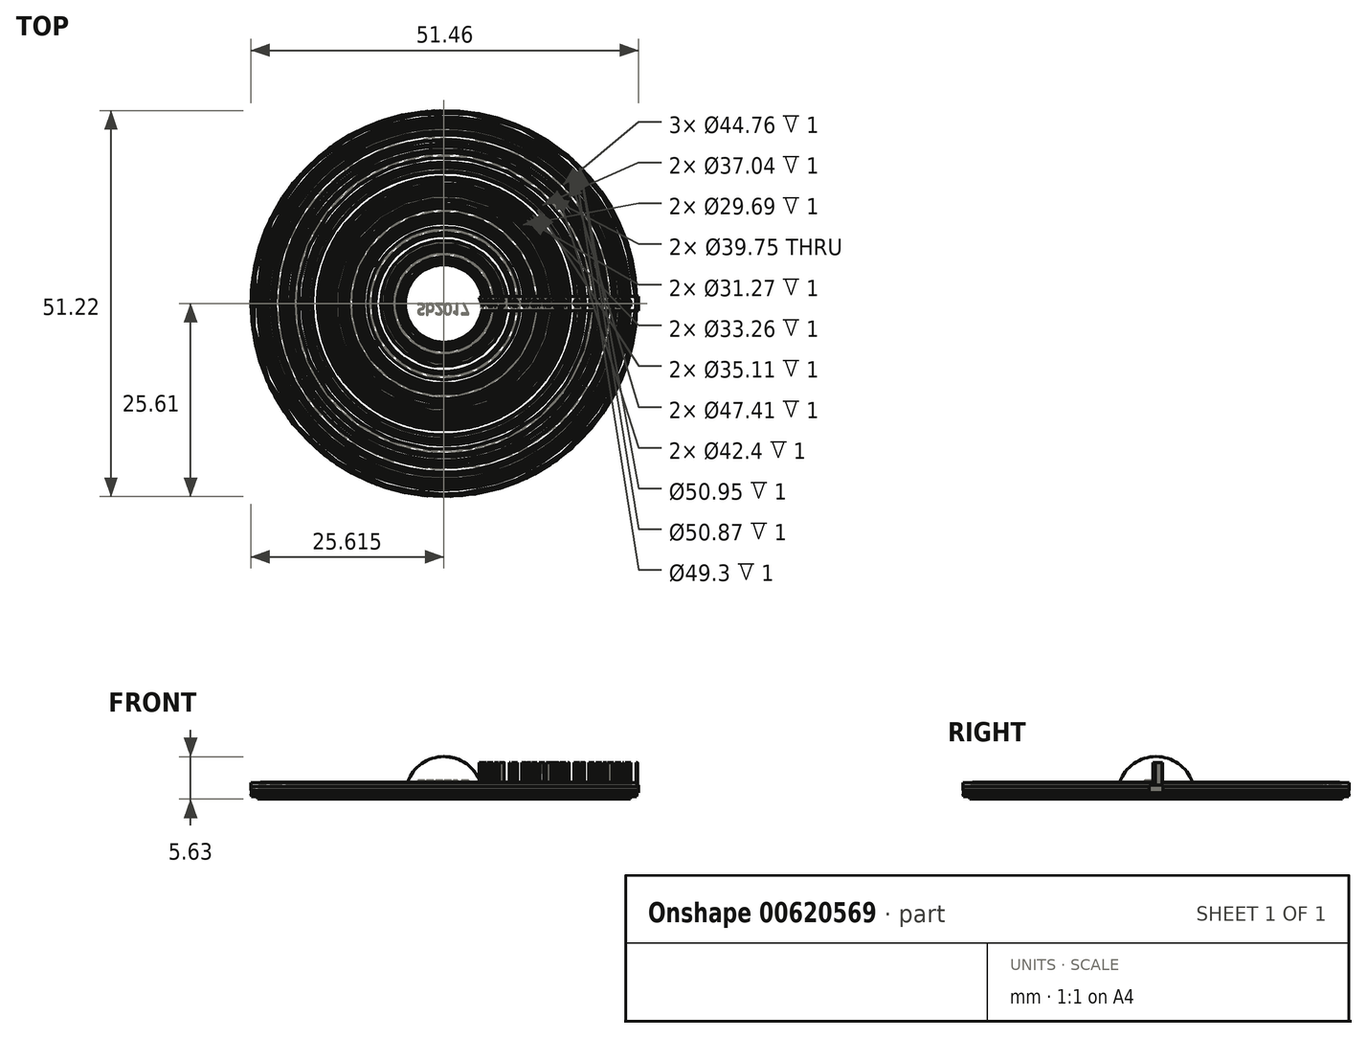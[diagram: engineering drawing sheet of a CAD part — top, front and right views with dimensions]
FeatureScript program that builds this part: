
annotation { "Feature Type Name" : "Feature", "Feature Type Description" : "" }
export const myFeature = defineFeature(function(context is Context, id is Id, definition is map)
    precondition{}
    {
        {
            var Q0;
            Q0=qCreatedBy(makeId("Front.planeOp"),FACE);
            var sketch = newSketch(context, id + "F0", { "sketchPlane" : qUnion([Q0])});
            skPoint(sketch, "E0", {"position": v(-19.14, 21.87) * mm});
            skText(sketch, "E1", { "text": "Vers le transfini et au-delà !", "fontName": "OpenSans-Regular.ttf"});
            skLineSegment(sketch, "E2", {"start": v(-14, 20.73) * mm, "end": v(-19.14, 20.73) * mm});
            skLineSegment(sketch, "E3", {"start": v(-14.14, 20.73) * mm, "end": v(-19.14, 20.73) * mm});
            skLineSegment(sketch, "E4", {"start": v(-19.14, 20.73) * mm, "end": v(-19.14, 25.86) * mm});
            skArc(sketch, "E5", {"start": v(-14, 20.73) * mm, "mid": v(-15.5, 24.36) * mm, "end": v(-19.14, 25.86) * mm});
            skLineSegment(sketch, "E6", {"start": v(-19.14, 25.86) * mm, "end": v(-19.14, 20.73) * mm});
            const initialGuessF0  = {"E1": [-0.014, 0.02073, 1, 0, 0.00117]};
            skSetInitialGuess(sketch, initialGuessF0);
            skSolve(sketch);
        }
        {
            var Q0;
            Q0=qSketchRegion(id+"F0",true);
            var Q1;
            Q1=sQuery(id+"F0.wireOp",EDGE,"E6");
            revolve(context, id + "F1", {"entities" : qUnion([Q0]), "axis" : qUnion([Q1]), "revolveType" : RevolveType.FULL});
        }
        {
            var Q0;
            Q0=makeQuery(id+"F1.opRevolve","SWEPT_FACE",FACE,{"disambiguationData":[OSD([sQuery(id+"F0.wireOp",EDGE,"E1.sketch_text.stroke-156")])]});
            var sketch = newSketch(context, id + "F2", { "sketchPlane" : qUnion([Q0])});
            skLineSegment(sketch, "E7.bottom", {"start": v(-14.29, 0.94) * mm, "end": v(6.71, 0.94) * mm});
            skLineSegment(sketch, "E7.top", {"start": v(-14.29, -0.94) * mm, "end": v(6.71, -0.94) * mm});
            skLineSegment(sketch, "E7.left", {"start": v(-14.29, 0.94) * mm, "end": v(-14.29, -0.94) * mm});
            skLineSegment(sketch, "E7.right", {"start": v(6.71, 0.94) * mm, "end": v(6.71, -0.94) * mm});
            skSolve(sketch);
        }
        {
            var Q0;
            Q0=makeQuery(id+"F2.imprint","IMPRINT",FACE,{"disambiguationData":[TD([[makeQuery(id+"F2.imprint","IMPRINT",EDGE,{"derivedFrom":sQuery(id+"F2.wireOp",EDGE,"E7.bottom")}),-1.0]])]});
            var Q1;
            Q1=makeQuery(id+"F1.opRevolve","SWEPT_FACE",FACE,{"disambiguationData":[OSD([sQuery(id+"F0.wireOp",EDGE,"E1.sketch_text.stroke-278")])]});
            var Q2;
            Q2=makeQuery(id+"F1.opRevolve","SWEPT_FACE",FACE,{"disambiguationData":[OSD([sQuery(id+"F0.wireOp",EDGE,"E1.sketch_text.stroke-280")])]});
            var Q3;
            Q3=makeQuery(id+"F1.opRevolve","SWEPT_FACE",FACE,{"disambiguationData":[OSD([sQuery(id+"F0.wireOp",EDGE,"E1.sketch_text.stroke-227")])]});
            var Q4;
            Q4=makeQuery(id+"F1.opRevolve","SWEPT_FACE",FACE,{"disambiguationData":[OSD([sQuery(id+"F0.wireOp",EDGE,"E1.sketch_text.stroke-238")])]});
            var Q5;
            Q5=makeQuery(id+"F1.opRevolve","SWEPT_FACE",FACE,{"disambiguationData":[OSD([sQuery(id+"F0.wireOp",EDGE,"E1.sketch_text.stroke-341")])]});
            var Q6;
            Q6=makeQuery(id+"F1.opRevolve","SWEPT_FACE",FACE,{"disambiguationData":[OSD([sQuery(id+"F0.wireOp",EDGE,"E1.sketch_text.stroke-345")])]});
            var Q7;
            Q7=makeQuery(id+"F1.opRevolve","SWEPT_FACE",FACE,{"disambiguationData":[OSD([sQuery(id+"F0.wireOp",EDGE,"E1.sketch_text.stroke-274")])]});
            var Q8;
            Q8=makeQuery(id+"F1.opRevolve","SWEPT_FACE",FACE,{"disambiguationData":[OSD([sQuery(id+"F0.wireOp",EDGE,"E1.sketch_text.stroke-282")])]});
            var Q9;
            Q9=makeQuery(id+"F1.opRevolve","SWEPT_FACE",FACE,{"disambiguationData":[OSD([sQuery(id+"F0.wireOp",EDGE,"E1.sketch_text.stroke-229")])]});
            var Q10;
            Q10=makeQuery(id+"F1.opRevolve","SWEPT_FACE",FACE,{"disambiguationData":[OSD([sQuery(id+"F0.wireOp",EDGE,"E1.sketch_text.stroke-255")])]});
            var Q11;
            Q11=makeQuery(id+"F1.opRevolve","SWEPT_FACE",FACE,{"disambiguationData":[OSD([sQuery(id+"F0.wireOp",EDGE,"E1.sketch_text.stroke-329")])]});
            var Q12;
            Q12=makeQuery(id+"F1.opRevolve","SWEPT_FACE",FACE,{"disambiguationData":[OSD([sQuery(id+"F0.wireOp",EDGE,"E1.sketch_text.stroke-319")])]});
            var Q13;
            Q13=makeQuery(id+"F1.opRevolve","SWEPT_FACE",FACE,{"disambiguationData":[OSD([sQuery(id+"F0.wireOp",EDGE,"E1.sketch_text.stroke-331")])]});
            var Q14;
            Q14=makeQuery(id+"F1.opRevolve","SWEPT_FACE",FACE,{"disambiguationData":[OSD([sQuery(id+"F0.wireOp",EDGE,"E1.sketch_text.stroke-418")])]});
            var Q15;
            Q15=makeQuery(id+"F1.opRevolve","SWEPT_FACE",FACE,{"disambiguationData":[OSD([sQuery(id+"F0.wireOp",EDGE,"E1.sketch_text.stroke-416")])]});
            var Q16;
            Q16=makeQuery(id+"F1.opRevolve","SWEPT_FACE",FACE,{"disambiguationData":[OSD([sQuery(id+"F0.wireOp",EDGE,"E1.sketch_text.stroke-379")])]});
            var Q17;
            Q17=makeQuery(id+"F1.opRevolve","SWEPT_FACE",FACE,{"disambiguationData":[OSD([sQuery(id+"F0.wireOp",EDGE,"E1.sketch_text.stroke-412")])]});
            var Q18;
            Q18=makeQuery(id+"F1.opRevolve","SWEPT_FACE",FACE,{"disambiguationData":[OSD([sQuery(id+"F0.wireOp",EDGE,"E1.sketch_text.stroke-205")])]});
            var Q19;
            Q19=makeQuery(id+"F1.opRevolve","SWEPT_FACE",FACE,{"disambiguationData":[OSD([sQuery(id+"F0.wireOp",EDGE,"E1.sketch_text.stroke-209")])]});
            var Q20;
            Q20=makeQuery(id+"F1.opRevolve","SWEPT_FACE",FACE,{"disambiguationData":[OSD([sQuery(id+"F0.wireOp",EDGE,"E1.sketch_text.stroke-235")])]});
            var Q21;
            Q21=makeQuery(id+"F1.opRevolve","SWEPT_FACE",FACE,{"disambiguationData":[OSD([sQuery(id+"F0.wireOp",EDGE,"E1.sketch_text.stroke-236")])]});
            var Q22;
            Q22=makeQuery(id+"F1.opRevolve","SWEPT_FACE",FACE,{"disambiguationData":[OSD([sQuery(id+"F0.wireOp",EDGE,"E1.sketch_text.stroke-264")])]});
            var Q23;
            Q23=makeQuery(id+"F1.opRevolve","SWEPT_FACE",FACE,{"disambiguationData":[OSD([sQuery(id+"F0.wireOp",EDGE,"E1.sketch_text.stroke-333")])]});
            var Q24;
            Q24=makeQuery(id+"F1.opRevolve","SWEPT_FACE",FACE,{"disambiguationData":[OSD([sQuery(id+"F0.wireOp",EDGE,"E1.sketch_text.stroke-408")])]});
            var Q25;
            Q25=makeQuery(id+"F1.opRevolve","SWEPT_FACE",FACE,{"disambiguationData":[OSD([sQuery(id+"F0.wireOp",EDGE,"E1.sketch_text.stroke-190")])]});
            var Q26;
            Q26=makeQuery(id+"F1.opRevolve","SWEPT_FACE",FACE,{"disambiguationData":[OSD([sQuery(id+"F0.wireOp",EDGE,"E1.sketch_text.stroke-323")])]});
            var Q27;
            Q27=makeQuery(id+"F1.opRevolve","SWEPT_FACE",FACE,{"disambiguationData":[OSD([sQuery(id+"F0.wireOp",EDGE,"E1.sketch_text.stroke-321")])]});
            var Q28;
            Q28=makeQuery(id+"F1.opRevolve","SWEPT_FACE",FACE,{"disambiguationData":[OSD([sQuery(id+"F0.wireOp",EDGE,"E1.sketch_text.stroke-377")])]});
            var Q29;
            Q29=makeQuery(id+"F1.opRevolve","SWEPT_FACE",FACE,{"disambiguationData":[OSD([sQuery(id+"F0.wireOp",EDGE,"E1.sketch_text.stroke-374")])]});
            var Q30;
            Q30=makeQuery(id+"F1.opRevolve","SWEPT_FACE",FACE,{"disambiguationData":[OSD([sQuery(id+"F0.wireOp",EDGE,"E1.sketch_text.stroke-365")])]});
            var Q31;
            Q31=makeQuery(id+"F1.opRevolve","SWEPT_FACE",FACE,{"disambiguationData":[OSD([sQuery(id+"F0.wireOp",EDGE,"E1.sketch_text.stroke-347")])]});
            var Q32;
            Q32=makeQuery(id+"F1.opRevolve","SWEPT_FACE",FACE,{"disambiguationData":[OSD([sQuery(id+"F0.wireOp",EDGE,"E1.sketch_text.stroke-334")])]});
            var Q33;
            Q33=makeQuery(id+"F1.opRevolve","SWEPT_FACE",FACE,{"disambiguationData":[OSD([sQuery(id+"F0.wireOp",EDGE,"E1.sketch_text.stroke-225")])]});
            var Q34;
            Q34=makeQuery(id+"F1.opRevolve","SWEPT_FACE",FACE,{"disambiguationData":[OSD([sQuery(id+"F0.wireOp",EDGE,"E1.sketch_text.stroke-304")])]});
            var Q35;
            Q35=makeQuery(id+"F1.opRevolve","SWEPT_FACE",FACE,{"disambiguationData":[OSD([sQuery(id+"F0.wireOp",EDGE,"E1.sketch_text.stroke-287")])]});
            var Q36;
            Q36=makeQuery(id+"F1.opRevolve","SWEPT_FACE",FACE,{"disambiguationData":[OSD([sQuery(id+"F0.wireOp",EDGE,"E1.sketch_text.stroke-399")])]});
            var Q37;
            Q37=makeQuery(id+"F1.opRevolve","SWEPT_FACE",FACE,{"disambiguationData":[OSD([sQuery(id+"F0.wireOp",EDGE,"E1.sketch_text.stroke-382")])]});
            extrude(context, id + "F3", {"entities" : qUnion([Q0, Q1, Q2, Q3, Q4, Q5, Q6, Q7, Q8, Q9, Q10, Q11, Q12, Q13, Q14, Q15, Q16, Q17, Q18, Q19, Q20, Q21, Q22, Q23, Q24, Q25, Q26, Q27, Q28, Q29, Q30, Q31, Q32, Q33, Q34, Q35, Q36, Q37]), "endBound" : BoundingType.SYMMETRIC, "depth" : 1 * mm, "offsetDistance" : 25 * mm});
        }
        {
            var Q0;
            Q0=makeQuery(id+"F3.opExtrude","CAP_FACE",FACE,{"disambiguationData":[OSD([sQuery(id+"F2.wireOp",EDGE,"E7.bottom"),sQuery(id+"F2.wireOp",EDGE,"E7.top"),sQuery(id+"F2.wireOp",EDGE,"E7.left"),sQuery(id+"F2.wireOp",EDGE,"E7.right")])],"isStart":false});
            var sketch = newSketch(context, id + "F4", { "sketchPlane" : qUnion([Q0])});
            skText(sketch, "E8", { "text": "Vers le transfini et au-delà !", "fontName": "OpenSans-Regular.ttf"});
            const initialGuessF4  = {"E8": [-0.01447, -0.0004, 1, 0, 0.0012]};
            skSetInitialGuess(sketch, initialGuessF4);
            skSolve(sketch);
        }
        {
            var Q0;
            Q0=qSketchRegion(id+"F4",true);
            var Q1;
            Q1 = qSketchRegion(id + "F6", true);
            extrude(context, id + "F5", {"entities" : qUnion([Q0, Q1]), "depth" : 3 * mm, "offsetDistance" : 25 * mm});
        }
        {
            var Q0;
            Q0=makeQuery(id+"F1.opRevolve","SWEPT_FACE",FACE,{"disambiguationData":[OSD([sQuery(id+"F0.wireOp",EDGE,"E2"),sQuery(id+"F0.wireOp",EDGE,"E3")])]});
            var sketch = newSketch(context, id + "F6", { "sketchPlane" : qUnion([Q0])});
            skText(sketch, "E9", { "text": "Sb2017", "fontName": "OpenSans-Regular.ttf"});
            const initialGuessF6  = {"E9": [-0.02272, 0, 1, 0, 0.00146]};
            skSetInitialGuess(sketch, initialGuessF6);
            skSolve(sketch);
        }
        {
            var Q0;
            Q0 = qSketchRegion(id + "F6", true);
            extrude(context, id + "F7", {"entities" : qUnion([Q0]), "operationType" : NewBodyOperationType.REMOVE, "oppositeDirection" : true, "depth" : 2 * mm, "offsetDistance" : 25 * mm});
        }
    });
